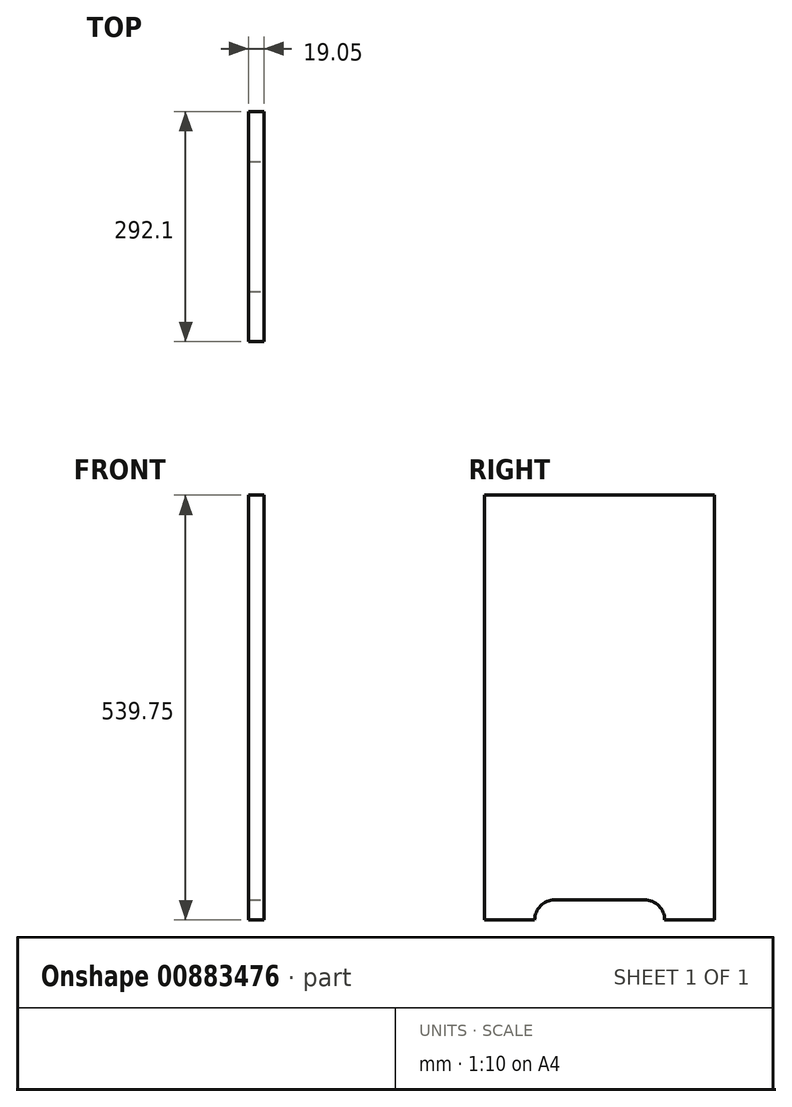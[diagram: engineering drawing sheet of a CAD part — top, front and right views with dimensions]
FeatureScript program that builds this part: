
annotation { "Feature Type Name" : "Feature", "Feature Type Description" : "" }
export const myFeature = defineFeature(function(context is Context, id is Id, definition is map)
    precondition{}
    {
        {
            var Q0;
            Q0=qCreatedBy(makeId("Right.planeOp"),FACE);
            var sketch = newSketch(context, id + "F0", { "sketchPlane" : qUnion([Q0])});
            skLineSegment(sketch, "E0.bottom", {"start": v(0, 0) * mm, "end": v(292.1, 0) * mm});
            skLineSegment(sketch, "E0.top", {"start": v(0, 539.75) * mm, "end": v(292.1, 539.75) * mm});
            skLineSegment(sketch, "E0.left", {"start": v(0, 0) * mm, "end": v(0, 539.75) * mm});
            skLineSegment(sketch, "E0.right", {"start": v(292.1, 0) * mm, "end": v(292.1, 539.75) * mm});
            skSolve(sketch);
        }
        {
            var Q0;
            Q0 = qSketchRegion(id + "F0", true);
            extrude(context, id + "F1", {"entities" : qUnion([Q0]), "depth" : 19.05 * mm, "offsetDistance" : 25.4 * mm});
        }
        {
            var Q0;
            Q0=makeQuery(id+"F1.opExtrude","CAP_FACE",FACE,{"disambiguationData":[OSD([sQuery(id+"F0.wireOp",EDGE,"E0.bottom"),sQuery(id+"F0.wireOp",EDGE,"E0.top"),sQuery(id+"F0.wireOp",EDGE,"E0.left"),sQuery(id+"F0.wireOp",EDGE,"E0.right")])],"isStart":false});
            var sketch = newSketch(context, id + "F2", { "sketchPlane" : qUnion([Q0])});
            skArc(sketch, "E1", {"start": v(88.9, 25.4) * mm, "mid": v(70.94, 17.96) * mm, "end": v(63.5, 0) * mm});
            skLineSegment(sketch, "E2", {"start": v(63.5, 0) * mm, "end": v(63.5, -128.64) * mm, "construction": true});
            skLineSegment(sketch, "E3", {"start": v(88.9, 25.4) * mm, "end": v(146.05, 25.4) * mm});
            skLineSegment(sketch, "E4", {"start": v(146.05, 0) * mm, "end": v(146.05, 539.75) * mm, "construction": true});
            skLineSegment(sketch, "E5.MirrorCS", {"start": v(203.2, 25.4) * mm, "end": v(146.05, 25.4) * mm});
            skArc(sketch, "E6.MirrorCS", {"start": v(203.2, 25.4) * mm, "mid": v(221.16, 17.96) * mm, "end": v(228.6, 0) * mm});
            skLineSegment(sketch, "E7", {"start": v(63.5, 0) * mm, "end": v(228.6, 0) * mm});
            skSolve(sketch);
        }
        {
            var Q0;
            Q0 = qSketchRegion(id + "F2", true);
            extrude(context, id + "F3", {"entities" : qUnion([Q0]), "operationType" : NewBodyOperationType.REMOVE, "oppositeDirection" : true, "depth" : 19.05 * mm, "offsetDistance" : 25.4 * mm});
        }
    });
